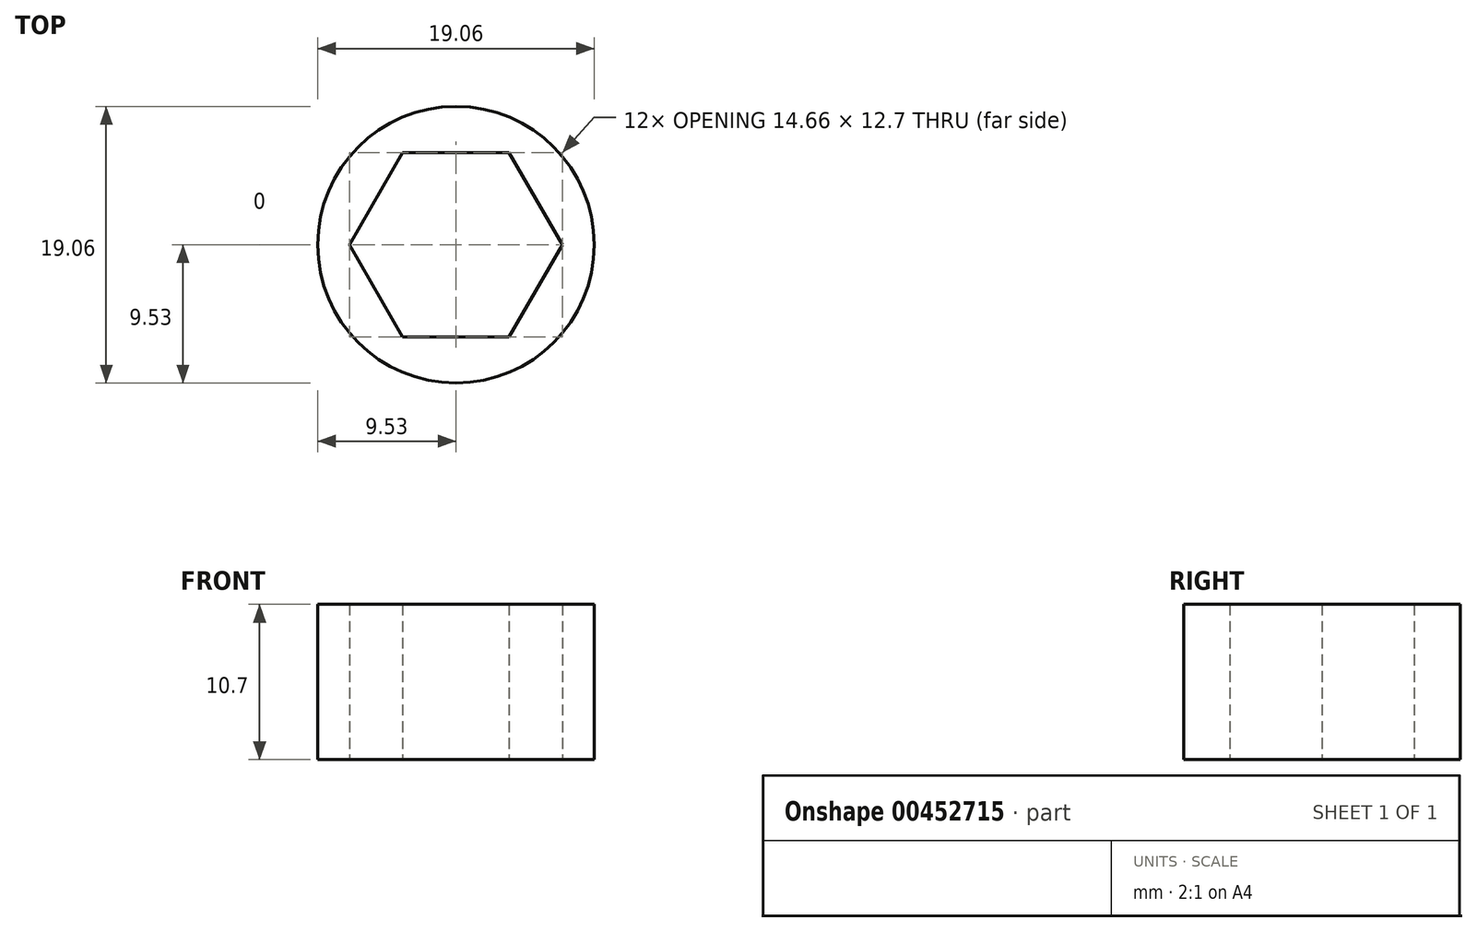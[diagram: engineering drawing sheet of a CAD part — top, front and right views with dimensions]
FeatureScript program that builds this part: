
annotation { "Feature Type Name" : "Feature", "Feature Type Description" : "" }
export const myFeature = defineFeature(function(context is Context, id is Id, definition is map)
    precondition{}
    {
        {
            var Q0;
            Q0=qCreatedBy(makeId("Top.planeOp"),FACE);
            var sketch = newSketch(context, id + "F0", { "sketchPlane" : qUnion([Q0])});
            skCircle(sketch, "E0.cCircle", {"center": v(0, 0) * mm, "radius": 6.35 * mm, "construction": true});
            skLineSegment(sketch, "E0.0", {"start": v(-3.67, 6.35) * mm, "end": v(3.67, 6.35) * mm});
            skLineSegment(sketch, "E0.1", {"start": v(3.67, 6.35) * mm, "end": v(7.33, 0) * mm});
            skLineSegment(sketch, "E0.2", {"start": v(7.33, 0) * mm, "end": v(3.67, -6.35) * mm});
            skLineSegment(sketch, "E0.3", {"start": v(3.67, -6.35) * mm, "end": v(-3.67, -6.35) * mm});
            skLineSegment(sketch, "E0.4", {"start": v(-3.67, -6.35) * mm, "end": v(-7.33, 0) * mm});
            skLineSegment(sketch, "E0.5", {"start": v(-7.33, 0) * mm, "end": v(-3.67, 6.35) * mm});
            skPoint(sketch, "E0.0.midPoint", {"position": v(0, 6.35) * mm});
            skCircle(sketch, "E1", {"center": v(0, 0) * mm, "radius": 9.53 * mm});
            skSolve(sketch);
        }
        {
            var Q0;
            Q0 = qSketchRegion(id + "F0", true);
            extrude(context, id + "F1", {"entities" : qUnion([Q0]), "depth" : 10.7 * mm});
        }
    });
